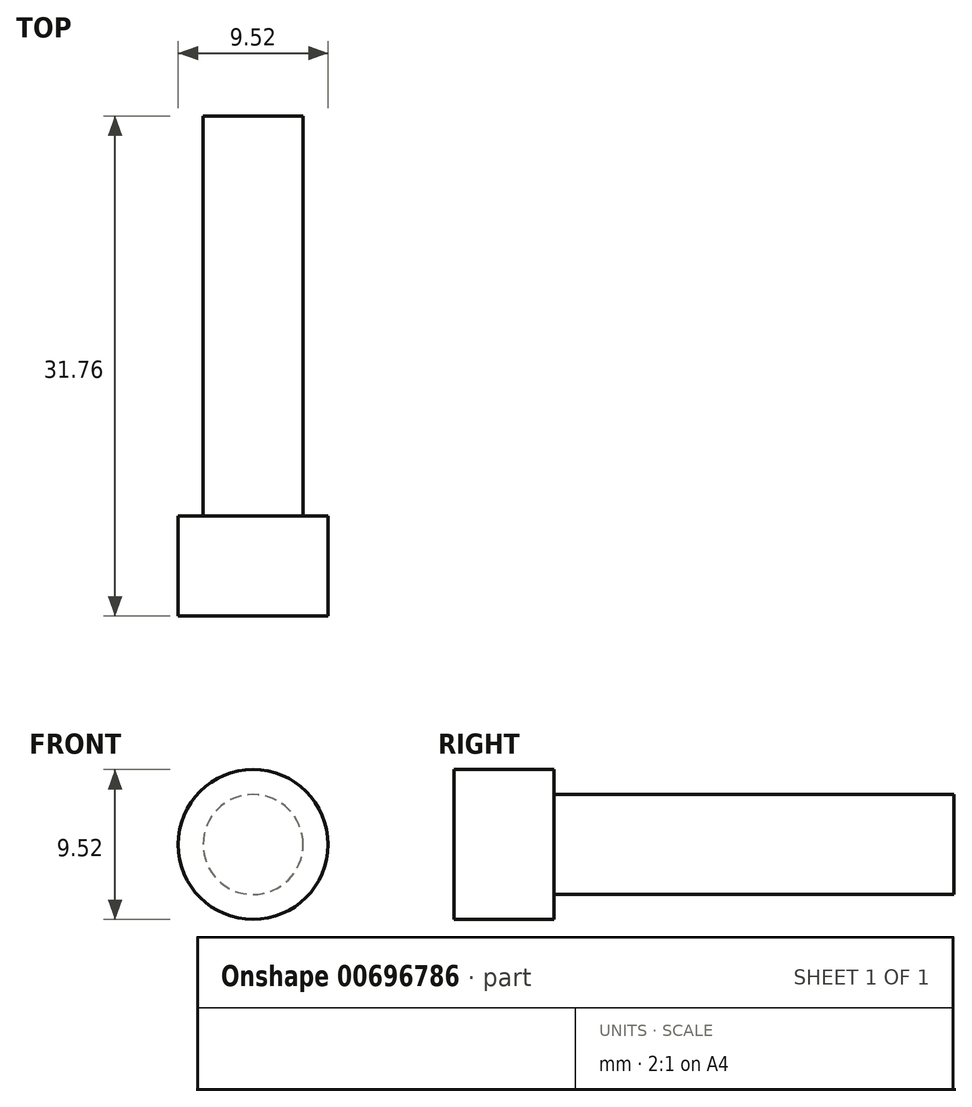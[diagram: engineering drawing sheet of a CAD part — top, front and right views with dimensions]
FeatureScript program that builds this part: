
annotation { "Feature Type Name" : "Feature", "Feature Type Description" : "" }
export const myFeature = defineFeature(function(context is Context, id is Id, definition is map)
    precondition{}
    {
        {
            var Q0;
            Q0=qCreatedBy(makeId("Front.planeOp"),FACE);
            var sketch = newSketch(context, id + "F0", { "sketchPlane" : qUnion([Q0])});
            skCircle(sketch, "E0", {"center": v(0, 0) * mm, "radius": 4.76 * mm});
            skSolve(sketch);
        }
        {
            var Q0;
            Q0=makeQuery(id+"F0.imprint","IMPRINT",FACE,{"disambiguationData":[TD([[makeQuery(id+"F0.imprint","IMPRINT",EDGE,{"derivedFrom":sQuery(id+"F0.wireOp",EDGE,"E0")}),1.0]])]});
            extrude(context, id + "F1", {"entities" : qUnion([Q0]), "depth" : 6.35 * mm, "offsetDistance" : 25.4 * mm, "symmetric" : true});
        }
        {
            var Q0;
            Q0=makeQuery(id+"F1.opExtrude","CAP_FACE",FACE,{"disambiguationData":[OSD([sQuery(id+"F0.wireOp",EDGE,"E0")])],"isStart":true});
            var sketch = newSketch(context, id + "F2", { "sketchPlane" : qUnion([Q0])});
            skCircle(sketch, "E1", {"center": v(0, 0) * mm, "radius": 3.18 * mm});
            skSolve(sketch);
        }
        {
            var Q0;
            Q0=makeQuery(id+"F2.imprint","IMPRINT",FACE,{"disambiguationData":[TD([[makeQuery(id+"F2.imprint","IMPRINT",EDGE,{"derivedFrom":sQuery(id+"F2.wireOp",EDGE,"E1")}),1.0]])]});
            extrude(context, id + "F3", {"entities" : qUnion([Q0]), "operationType" : NewBodyOperationType.ADD, "depth" : 25.4 * mm, "offsetDistance" : 25.4 * mm});
        }
    });
